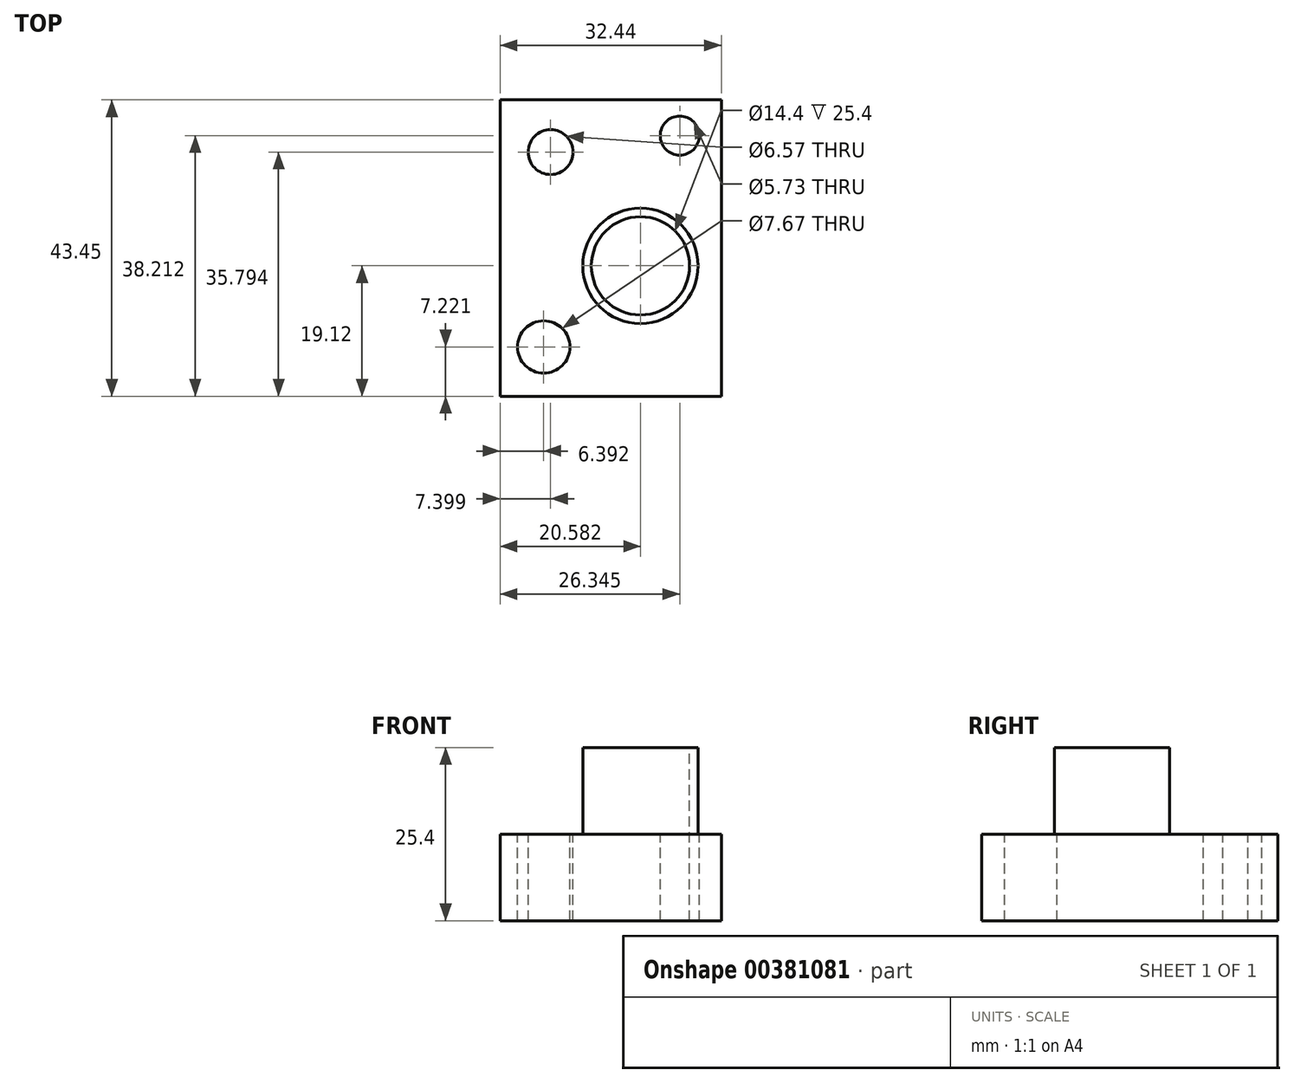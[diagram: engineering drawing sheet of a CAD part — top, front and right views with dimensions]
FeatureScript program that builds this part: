
annotation { "Feature Type Name" : "Feature", "Feature Type Description" : "" }
export const myFeature = defineFeature(function(context is Context, id is Id, definition is map)
    precondition{}
    {
        {
            var Q0;
            Q0=qCreatedBy(makeId("Top.planeOp"),FACE);
            var sketch = newSketch(context, id + "F0", { "sketchPlane" : qUnion([Q0])});
            skLineSegment(sketch, "E0.bottom", {"start": v(-33.55, 16.68) * mm, "end": v(-66, 16.68) * mm});
            skLineSegment(sketch, "E0.top", {"start": v(-33.55, 60.13) * mm, "end": v(-66, 60.13) * mm});
            skLineSegment(sketch, "E0.left", {"start": v(-33.55, 16.68) * mm, "end": v(-33.55, 60.13) * mm});
            skLineSegment(sketch, "E0.right", {"start": v(-66, 16.68) * mm, "end": v(-66, 60.13) * mm});
            skSolve(sketch);
        }
        {
            var Q0;
            Q0=makeQuery(id+"F0.imprint","IMPRINT",FACE,{"disambiguationData":[TD([[makeQuery(id+"F0.imprint","IMPRINT",EDGE,{"derivedFrom":sQuery(id+"F0.wireOp",EDGE,"E0.bottom")}),-1.0]])]});
            extrude(context, id + "F1", {"entities" : qUnion([Q0]), "depth" : 12.7 * mm});
        }
        {
            var Q0;
            Q0=makeQuery(id+"F1.opExtrude","CAP_FACE",FACE,{"disambiguationData":[OSD([sQuery(id+"F0.wireOp",EDGE,"E0.bottom"),sQuery(id+"F0.wireOp",EDGE,"E0.top"),sQuery(id+"F0.wireOp",EDGE,"E0.left"),sQuery(id+"F0.wireOp",EDGE,"E0.right")])],"isStart":false});
            var sketch = newSketch(context, id + "F2", { "sketchPlane" : qUnion([Q0])});
            skCircle(sketch, "E1", {"center": v(-45.4, 35.8) * mm, "radius": 8.46 * mm});
            skSolve(sketch);
        }
        {
            var Q0;
            Q0=makeQuery(id+"F2.imprint","IMPRINT",FACE,{"disambiguationData":[TD([[makeQuery(id+"F2.imprint","IMPRINT",EDGE,{"derivedFrom":sQuery(id+"F2.wireOp",EDGE,"E1")}),1.0]])]});
            extrude(context, id + "F3", {"entities" : qUnion([Q0]), "operationType" : NewBodyOperationType.ADD, "depth" : 12.7 * mm});
        }
        {
            var Q0;
            Q0=makeQuery(id+"F3.opExtrude","CAP_FACE",FACE,{"disambiguationData":[OSD([sQuery(id+"F2.wireOp",EDGE,"E1")])],"isStart":false});
            var sketch = newSketch(context, id + "F4", { "sketchPlane" : qUnion([Q0])});
            skCircle(sketch, "E2", {"center": v(-45.4, 35.8) * mm, "radius": 7.2 * mm});
            skSolve(sketch);
        }
        {
            var Q0;
            Q0=makeQuery(id+"F4.imprint","IMPRINT",FACE,{"disambiguationData":[TD([[makeQuery(id+"F4.imprint","IMPRINT",EDGE,{"derivedFrom":sQuery(id+"F4.wireOp",EDGE,"E2")}),1.0]])]});
            extrude(context, id + "F5", {"entities" : qUnion([Q0]), "operationType" : NewBodyOperationType.REMOVE, "oppositeDirection" : true, "depth" : 25.4 * mm});
        }
        {
            var Q0;
            Q0=makeQuery(id+"F1.opExtrude","CAP_FACE",FACE,{"disambiguationData":[OSD([sQuery(id+"F0.wireOp",EDGE,"E0.bottom"),sQuery(id+"F0.wireOp",EDGE,"E0.top"),sQuery(id+"F0.wireOp",EDGE,"E0.left"),sQuery(id+"F0.wireOp",EDGE,"E0.right")])],"isStart":false});
            var sketch = newSketch(context, id + "F6", { "sketchPlane" : qUnion([Q0])});
            skSolve(sketch);
        }
        {
            var Q0;
            Q0=makeQuery(id+"F6.imprint","IMPRINT",FACE,{"disambiguationData":[TD([[makeQuery(id+"F6.imprint","IMPRINT",EDGE,{"derivedFrom":makeQuery(id+"F1.opExtrude","CAP_EDGE",EDGE,{"disambiguationData":[OSD([sQuery(id+"F0.wireOp",EDGE,"E0.bottom")])],"isStart":false})}),-1.0]])]});
            var sketch = newSketch(context, id + "F7", { "sketchPlane" : qUnion([Q0])});
            skSolve(sketch);
        }
        {
            var Q0;
            Q0=makeQuery(id+"F6.imprint","IMPRINT",FACE,{"disambiguationData":[TD([[makeQuery(id+"F6.imprint","IMPRINT",EDGE,{"derivedFrom":makeQuery(id+"F1.opExtrude","CAP_EDGE",EDGE,{"disambiguationData":[OSD([sQuery(id+"F0.wireOp",EDGE,"E0.bottom")])],"isStart":false})}),-1.0]])]});
            var sketch = newSketch(context, id + "F8", { "sketchPlane" : qUnion([Q0])});
            skCircle(sketch, "E3", {"center": v(-58.6, 52.47) * mm, "radius": 3.29 * mm});
            skSolve(sketch);
        }
        {
            var Q0;
            Q0 = qSketchRegion(id + "F8", true);
            extrude(context, id + "F9", {"entities" : qUnion([Q0]), "operationType" : NewBodyOperationType.REMOVE, "oppositeDirection" : true, "depth" : 25.4 * mm});
        }
        {
            var Q0;
            Q0=makeQuery(id+"F6.imprint","IMPRINT",FACE,{"disambiguationData":[TD([[makeQuery(id+"F6.imprint","IMPRINT",EDGE,{"derivedFrom":makeQuery(id+"F1.opExtrude","CAP_EDGE",EDGE,{"disambiguationData":[OSD([sQuery(id+"F0.wireOp",EDGE,"E0.bottom")])],"isStart":false})}),-1.0]])]});
            var sketch = newSketch(context, id + "F10", { "sketchPlane" : qUnion([Q0])});
            skCircle(sketch, "E4", {"center": v(-39.64, 54.9) * mm, "radius": 2.87 * mm});
            skSolve(sketch);
        }
        {
            var Q0;
            Q0 = qSketchRegion(id + "F10", true);
            extrude(context, id + "F11", {"entities" : qUnion([Q0]), "operationType" : NewBodyOperationType.REMOVE, "oppositeDirection" : true, "depth" : 25.4 * mm});
        }
        {
            var Q0;
            Q0=makeQuery(id+"F7.imprint","IMPRINT",FACE,{"disambiguationData":[TD([[makeQuery(id+"F7.imprint","IMPRINT",EDGE,{"derivedFrom":makeQuery(id+"F6.imprint","IMPRINT",EDGE,{"derivedFrom":makeQuery(id+"F1.opExtrude","CAP_EDGE",EDGE,{"disambiguationData":[OSD([sQuery(id+"F0.wireOp",EDGE,"E0.bottom")])],"isStart":false})})}),-1.0]])]});
            var sketch = newSketch(context, id + "F12", { "sketchPlane" : qUnion([Q0])});
            skCircle(sketch, "E5", {"center": v(-59.6, 23.9) * mm, "radius": 3.83 * mm});
            skSolve(sketch);
        }
        {
            var Q0;
            Q0 = qSketchRegion(id + "F12", true);
            extrude(context, id + "F13", {"entities" : qUnion([Q0]), "operationType" : NewBodyOperationType.REMOVE, "oppositeDirection" : true, "depth" : 25.4 * mm});
        }
    });
